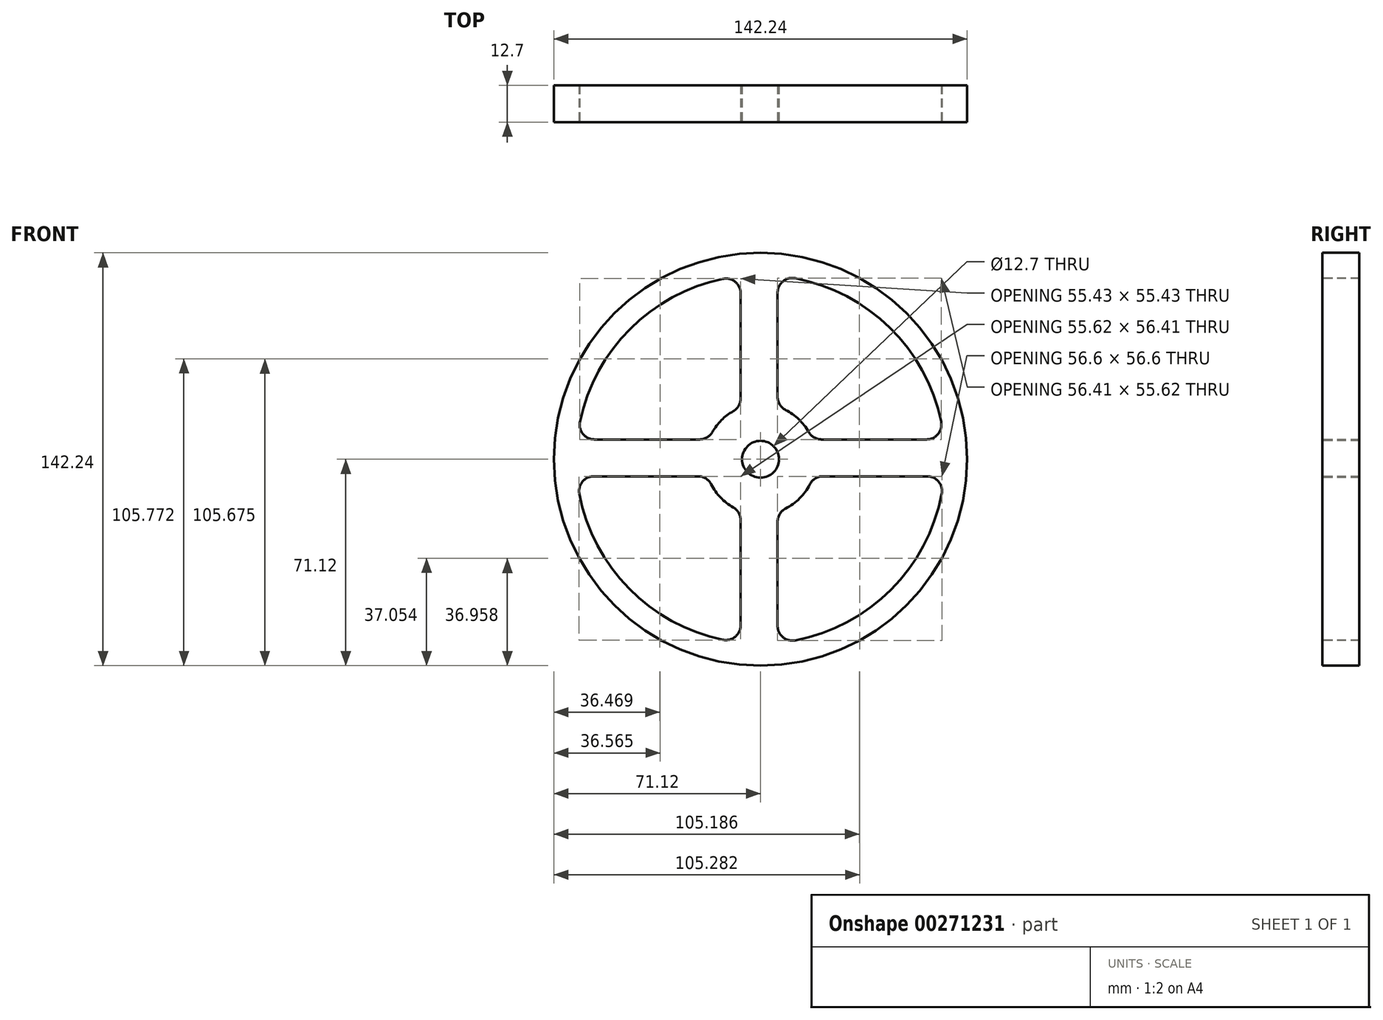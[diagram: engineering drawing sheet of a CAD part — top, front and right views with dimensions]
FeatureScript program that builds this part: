
annotation { "Feature Type Name" : "Feature", "Feature Type Description" : "" }
export const myFeature = defineFeature(function(context is Context, id is Id, definition is map)
    precondition{}
    {
        {
            var Q0;
            Q0=qCreatedBy(makeId("Front.planeOp"),FACE);
            var sketch = newSketch(context, id + "F0", { "sketchPlane" : qUnion([Q0])});
            skArc(sketch, "E0", {"start": v(-12.96, 62.16) * mm, "mid": v(-44.9, 44.9) * mm, "end": v(-62.16, 12.96) * mm});
            skCircle(sketch, "E1", {"center": v(0, 0) * mm, "radius": 71.12 * mm});
            skArc(sketch, "E2", {"start": v(-9.4, 16.56) * mm, "mid": v(-13.47, 13.47) * mm, "end": v(-16.56, 9.4) * mm});
            skCircle(sketch, "E3", {"center": v(0, 0) * mm, "radius": 6.35 * mm});
            skCircle(sketch, "E4", {"center": v(0, 0) * mm, "radius": 12.7 * mm});
            skLineSegment(sketch, "E5", {"start": v(5.86, 21.5) * mm, "end": v(5.86, 57.39) * mm});
            skLineSegment(sketch, "E6", {"start": v(-6.84, 20.98) * mm, "end": v(-6.84, 57.2) * mm});
            skLineSegment(sketch, "E7", {"start": v(-6.84, -20.98) * mm, "end": v(-6.84, -57.2) * mm});
            skLineSegment(sketch, "E8", {"start": v(5.86, -57.39) * mm, "end": v(5.86, -21.5) * mm});
            skLineSegment(sketch, "E9", {"start": v(20.98, 6.84) * mm, "end": v(57.2, 6.84) * mm});
            skLineSegment(sketch, "E10", {"start": v(21.5, -5.86) * mm, "end": v(57.39, -5.86) * mm});
            skLineSegment(sketch, "E11", {"start": v(-20.98, 6.84) * mm, "end": v(-57.2, 6.84) * mm});
            skLineSegment(sketch, "E12", {"start": v(-21.5, -5.86) * mm, "end": v(-57.39, -5.86) * mm});
            skArc(sketch, "E13.trimOffspring", {"start": v(62.16, 12.96) * mm, "mid": v(44.52, 45.28) * mm, "end": v(11.9, 62.38) * mm});
            skArc(sketch, "E14.trimOffspring", {"start": v(-62.38, -11.9) * mm, "mid": v(-45.28, -44.52) * mm, "end": v(-12.96, -62.16) * mm});
            skArc(sketch, "E15.trimOffspring", {"start": v(16.56, 9.4) * mm, "mid": v(13.16, 13.78) * mm, "end": v(8.64, 16.98) * mm});
            skArc(sketch, "E16.trimOffspring", {"start": v(8.64, -16.98) * mm, "mid": v(13.47, -13.47) * mm, "end": v(16.98, -8.64) * mm});
            skArc(sketch, "E17.trimOffspring", {"start": v(-16.98, -8.64) * mm, "mid": v(-13.78, -13.16) * mm, "end": v(-9.4, -16.56) * mm});
            skPoint(sketch, "E18.visualSharp", {"position": v(-6.84, 63.13) * mm});
            skArc(sketch, "E18.filletArc", {"start": v(-6.84, 57.2) * mm, "mid": v(-8.71, 61.13) * mm, "end": v(-12.96, 62.16) * mm});
            skPoint(sketch, "E19.visualSharp", {"position": v(5.86, 63.23) * mm});
            skArc(sketch, "E19.filletArc", {"start": v(11.9, 62.38) * mm, "mid": v(7.7, 61.3) * mm, "end": v(5.86, 57.39) * mm});
            skPoint(sketch, "E20.visualSharp", {"position": v(63.13, 6.84) * mm});
            skArc(sketch, "E20.filletArc", {"start": v(57.2, 6.84) * mm, "mid": v(61.13, 8.71) * mm, "end": v(62.16, 12.96) * mm});
            skPoint(sketch, "E21.visualSharp", {"position": v(63.23, -5.86) * mm});
            skArc(sketch, "E21.filletArc", {"start": v(62.38, -11.9) * mm, "mid": v(61.3, -7.7) * mm, "end": v(57.39, -5.86) * mm});
            skArc(sketch, "E22.trimOffspring", {"start": v(11.9, -62.38) * mm, "mid": v(44.9, -44.9) * mm, "end": v(62.38, -11.9) * mm});
            skPoint(sketch, "E23.visualSharp", {"position": v(5.86, -63.23) * mm});
            skArc(sketch, "E23.filletArc", {"start": v(5.86, -57.39) * mm, "mid": v(7.7, -61.3) * mm, "end": v(11.9, -62.38) * mm});
            skPoint(sketch, "E24.visualSharp", {"position": v(-6.84, -63.13) * mm});
            skArc(sketch, "E24.filletArc", {"start": v(-12.96, -62.16) * mm, "mid": v(-8.71, -61.13) * mm, "end": v(-6.84, -57.2) * mm});
            skPoint(sketch, "E25.visualSharp", {"position": v(-63.23, -5.86) * mm});
            skArc(sketch, "E25.filletArc", {"start": v(-57.39, -5.86) * mm, "mid": v(-61.3, -7.7) * mm, "end": v(-62.38, -11.9) * mm});
            skPoint(sketch, "E26.visualSharp", {"position": v(-63.13, 6.84) * mm});
            skArc(sketch, "E26.filletArc", {"start": v(-62.16, 12.96) * mm, "mid": v(-61.13, 8.71) * mm, "end": v(-57.2, 6.84) * mm});
            skPoint(sketch, "E27.visualSharp", {"position": v(-17.78, 6.84) * mm});
            skArc(sketch, "E27.filletArc", {"start": v(-20.98, 6.84) * mm, "mid": v(-18.43, 7.53) * mm, "end": v(-16.56, 9.4) * mm});
            skPoint(sketch, "E28.visualSharp", {"position": v(-6.84, 17.78) * mm});
            skArc(sketch, "E28.filletArc", {"start": v(-9.4, 16.56) * mm, "mid": v(-7.53, 18.43) * mm, "end": v(-6.84, 20.98) * mm});
            skPoint(sketch, "E29.visualSharp", {"position": v(-18.13, -5.86) * mm});
            skArc(sketch, "E29.filletArc", {"start": v(-16.98, -8.64) * mm, "mid": v(-18.85, -6.61) * mm, "end": v(-21.5, -5.86) * mm});
            skPoint(sketch, "E30.visualSharp", {"position": v(-6.84, -17.78) * mm});
            skArc(sketch, "E30.filletArc", {"start": v(-6.84, -20.98) * mm, "mid": v(-7.53, -18.43) * mm, "end": v(-9.4, -16.56) * mm});
            skPoint(sketch, "E31.visualSharp", {"position": v(5.86, -18.13) * mm});
            skArc(sketch, "E31.filletArc", {"start": v(8.64, -16.98) * mm, "mid": v(6.61, -18.85) * mm, "end": v(5.86, -21.5) * mm});
            skPoint(sketch, "E32.visualSharp", {"position": v(18.13, -5.86) * mm});
            skArc(sketch, "E32.filletArc", {"start": v(21.5, -5.86) * mm, "mid": v(18.85, -6.61) * mm, "end": v(16.98, -8.64) * mm});
            skPoint(sketch, "E33.visualSharp", {"position": v(17.78, 6.84) * mm});
            skArc(sketch, "E33.filletArc", {"start": v(16.56, 9.4) * mm, "mid": v(18.43, 7.53) * mm, "end": v(20.98, 6.84) * mm});
            skPoint(sketch, "E34.visualSharp", {"position": v(5.86, 18.13) * mm});
            skArc(sketch, "E34.filletArc", {"start": v(5.86, 21.5) * mm, "mid": v(6.61, 18.85) * mm, "end": v(8.64, 16.98) * mm});
            skSolve(sketch);
        }
        {
            var Q0;
            Q0 = qSketchRegion(id + "F0", true);
            var Q1;
            Q1=makeQuery(id+"F0.imprint","IMPRINT",FACE,{"disambiguationData":[TD([[makeQuery(id+"F0.imprint","IMPRINT",EDGE,{"derivedFrom":sQuery(id+"F0.wireOp",EDGE,"E3")}),-1.0]])]});
            extrude(context, id + "F1", {"entities" : qUnion([Q0, Q1]), "oppositeDirection" : true, "depth" : 12.7 * mm});
        }
    });
